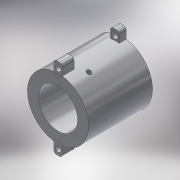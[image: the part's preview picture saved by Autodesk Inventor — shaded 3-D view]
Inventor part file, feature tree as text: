
AUTODESK INVENTOR PART (.ipt)
format: ipt  version: 2018.2 (Build 222227000, 227)  size: 247,296 bytes
history: native  units: in
note: dims shown in document units (in); Inventor stores cm internally (conversion verified against a paired STEP export)
features: extrude x2, sketch x2, direct_edit x1, pattern_circular x1, mirror x1, move_body x1
ambient origin geometry x8: Origin, YZ Plane, XZ Plane, XY Plane, X Axis, Y Axis, Z Axis, Center Point
bodies: Solid1 (feature_tree)
feature tree (8):
  direct_edit  "Direct Edit1"
  extrude  "Extrusion1"  Depth=0.0787in
  extrude  "Extrusion2"  Depth=0.1575in TaperAngle=0.0deg
  pattern_circular  "Circular Pattern1"  [2 undecoded]
  sketch  "Sketch2"  dims[d0=0.0in d1=0.0in d2=0.1181in d3=0.0787in]
  sketch  "Sketch3"  dims[d4=0.1969in d5=0.1575in d6=0.0in d7=0.1339in d8=0.0492in d9=0.6693in d10=0.6693in d11=0.0in d12=0.0in d13=0.7874in d14=360.0deg]
  mirror  "Mirror7"
  move_body  "Move1"
note: 2 required parameter values undecoded (feature->parameter linkage not recoverable at this tier; creation-order binding heuristic only, values carry confidence <= 0.55)
